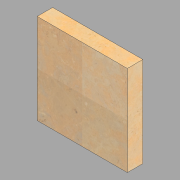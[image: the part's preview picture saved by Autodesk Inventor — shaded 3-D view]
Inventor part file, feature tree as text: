
AUTODESK INVENTOR PART (.ipt)
format: ipt  version: 2022.1 (Build 261234020, 234B)  size: 108,032 bytes
history: native  units: in
note: dims shown in document units (in); Inventor stores cm internally (conversion verified against a paired STEP export)
features: extrude x1, sketch x1
ambient origin geometry x8: Origin, YZ Plane, XZ Plane, XY Plane, X Axis, Y Axis, Z Axis, Center Point
bodies: Solid1 (feature_tree)
feature tree (2):
  extrude  "Extrusion1"  Depth=11.625in
  sketch  "Sketch1"  dims[d0=11.625in d1=11.625in d2=2.0in d3=0.0in]
